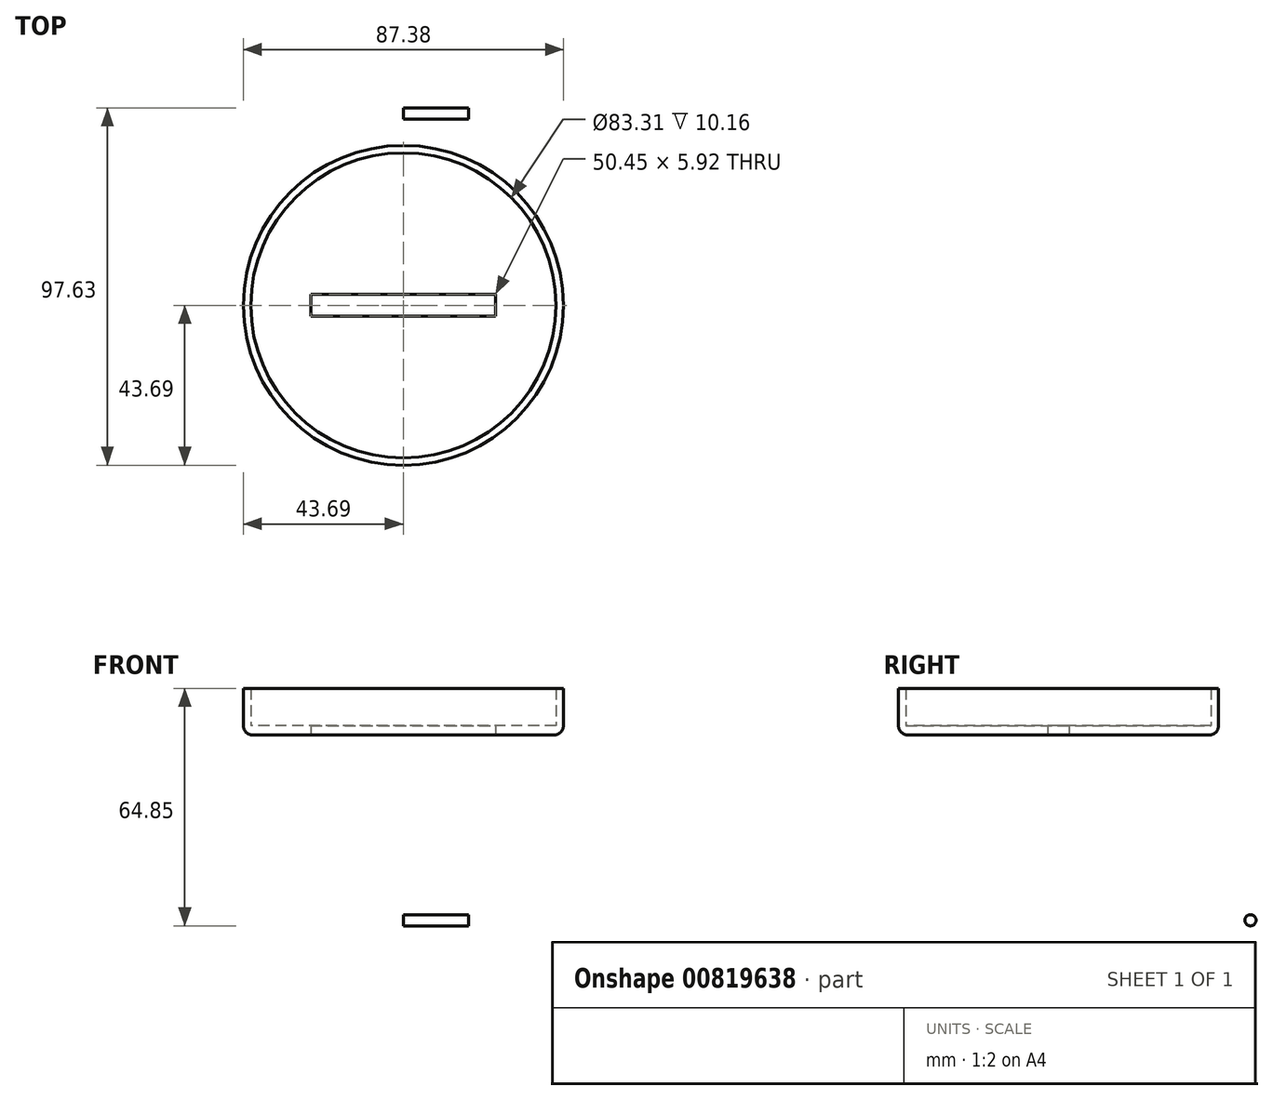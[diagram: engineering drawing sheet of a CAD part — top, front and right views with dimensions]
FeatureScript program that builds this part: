
annotation { "Feature Type Name" : "Feature", "Feature Type Description" : "" }
export const myFeature = defineFeature(function(context is Context, id is Id, definition is map)
    precondition{}
    {
        {
            var Q0;
            Q0=qCreatedBy(makeId("Top.planeOp"),FACE);
            var sketch = newSketch(context, id + "F0", { "sketchPlane" : qUnion([Q0])});
            skCircle(sketch, "E0", {"center": v(0, 0) * mm, "radius": 41.66 * mm});
            skCircle(sketch, "E1", {"center": v(0, 0) * mm, "radius": 43.69 * mm});
            skSolve(sketch);
        }
        {
            var Q0;
            Q0=makeQuery(id+"F0.imprint","IMPRINT",FACE,{"disambiguationData":[TD([[makeQuery(id+"F0.imprint","IMPRINT",EDGE,{"derivedFrom":sQuery(id+"F0.wireOp",EDGE,"E0")}),-1.0]])]});
            extrude(context, id + "F1", {"entities" : qUnion([Q0]), "depth" : 12.7 * mm, "offsetDistance" : 25.4 * mm});
        }
        {
            var Q0;
            Q0=makeQuery(id+"F0.imprint","IMPRINT",FACE,{"disambiguationData":[TD([[makeQuery(id+"F0.imprint","IMPRINT",EDGE,{"derivedFrom":sQuery(id+"F0.wireOp",EDGE,"E0")}),1.0]])]});
            extrude(context, id + "F2", {"entities" : qUnion([Q0]), "operationType" : NewBodyOperationType.ADD, "depth" : 2.54 * mm, "offsetDistance" : 25.4 * mm});
        }
        {
            var Q0;
            Q0=makeQuery(id+"F2.opExtrude","CAP_EDGE",EDGE,{"disambiguationData":[OSD([sQuery(id+"F0.wireOp",EDGE,"E0")])],"isStart":false});
            var Q1;
            Q1=makeQuery(id+"F1.opExtrude","CAP_EDGE",EDGE,{"disambiguationData":[OSD([sQuery(id+"F0.wireOp",EDGE,"E1")])],"isStart":true});
            fillet(context, id + "F3", {"entities" : qUnion([Q0, Q1]), "radius" : 2.54 * mm, "tangentPropagation" : true, "allowEdgeOverflow" : false});
        }
        {
            var Q0;
            Q0=qCreatedBy(makeId("Right.planeOp"),FACE);
            var sketch = newSketch(context, id + "F4", { "sketchPlane" : qUnion([Q0])});
            skCircle(sketch, "E2", {"center": v(52.41, -50.63) * mm, "radius": 1.52 * mm});
            skSolve(sketch);
        }
        {
            var Q0;
            Q0=makeQuery(id+"F4.imprint","IMPRINT",FACE,{"disambiguationData":[TD([[makeQuery(id+"F4.imprint","IMPRINT",EDGE,{"derivedFrom":sQuery(id+"F4.wireOp",EDGE,"E2")}),1.0]])]});
            extrude(context, id + "F5", {"entities" : qUnion([Q0]), "depth" : 17.78 * mm, "offsetDistance" : 25.4 * mm});
        }
        {
            var Q0;
            Q0=makeQuery(id+"F0.imprint","IMPRINT",FACE,{"disambiguationData":[TD([[makeQuery(id+"F0.imprint","IMPRINT",EDGE,{"derivedFrom":sQuery(id+"F0.wireOp",EDGE,"E0")}),1.0]])]});
            var sketch = newSketch(context, id + "F6", { "sketchPlane" : qUnion([Q0])});
            skLineSegment(sketch, "E3.bottom", {"start": v(25.23, -2.96) * mm, "end": v(-25.23, -2.96) * mm});
            skLineSegment(sketch, "E3.top", {"start": v(25.23, 2.96) * mm, "end": v(-25.23, 2.96) * mm});
            skLineSegment(sketch, "E3.left", {"start": v(25.23, -2.96) * mm, "end": v(25.23, 2.96) * mm});
            skLineSegment(sketch, "E3.right", {"start": v(-25.23, -2.96) * mm, "end": v(-25.23, 2.96) * mm});
            skPoint(sketch, "E3.middle", {"position": v(0, 0) * mm});
            skSolve(sketch);
        }
        {
            var Q0;
            Q0=makeQuery(id+"F6.imprint","IMPRINT",FACE,{"disambiguationData":[TD([[makeQuery(id+"F6.imprint","IMPRINT",EDGE,{"derivedFrom":sQuery(id+"F6.wireOp",EDGE,"E3.bottom")}),-1.0]])]});
            extrude(context, id + "F7", {"entities" : qUnion([Q0]), "operationType" : NewBodyOperationType.REMOVE, "depth" : 25.4 * mm, "offsetDistance" : 25.4 * mm});
        }
    });
